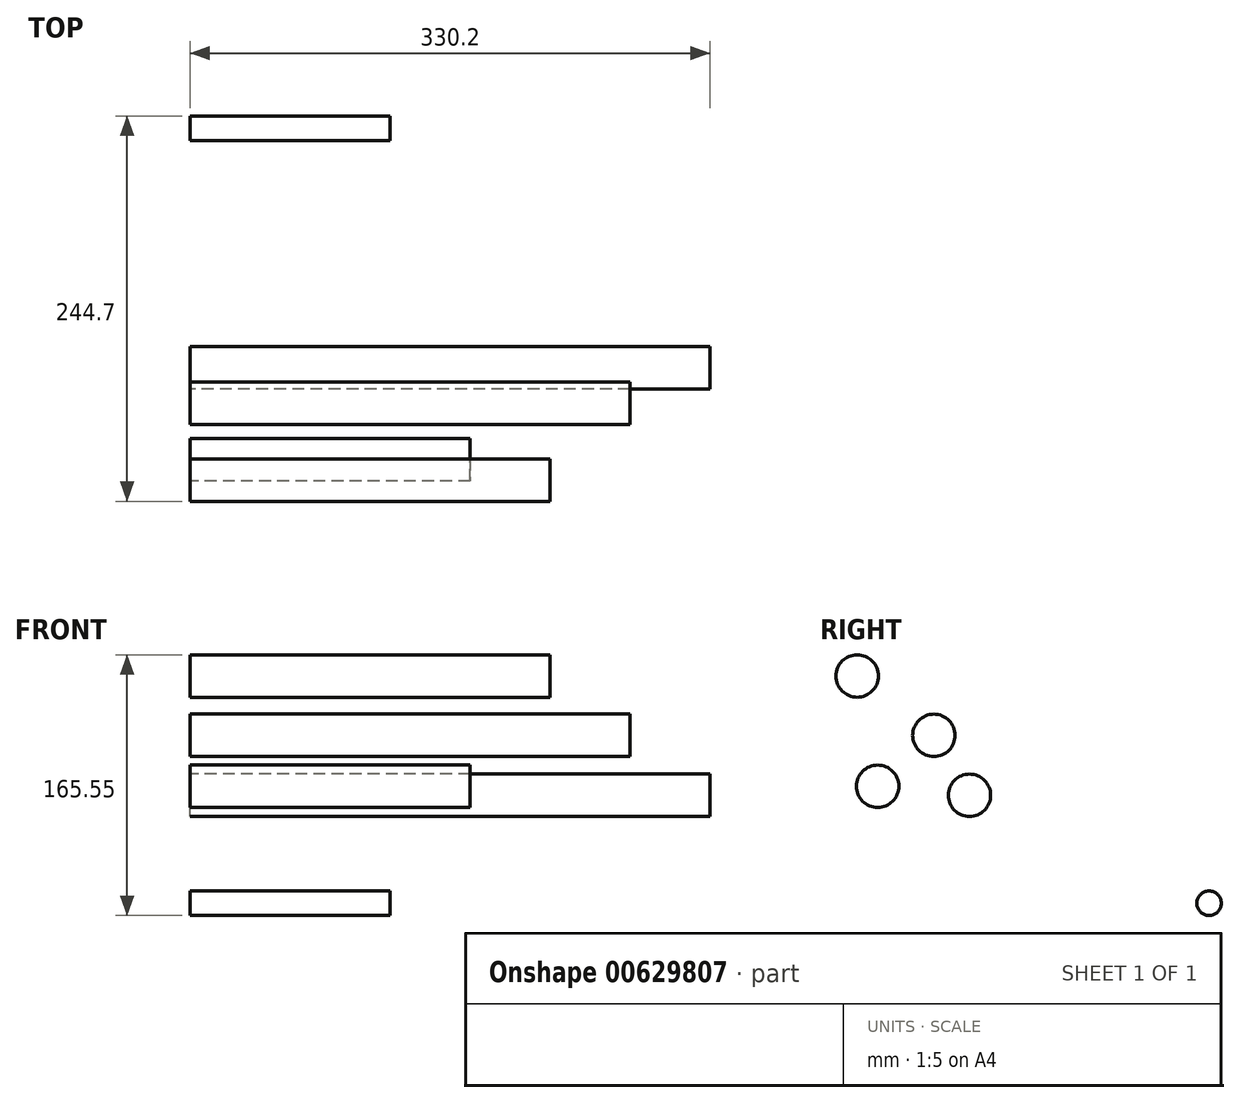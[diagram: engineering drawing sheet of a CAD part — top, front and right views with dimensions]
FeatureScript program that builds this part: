
annotation { "Feature Type Name" : "Feature", "Feature Type Description" : "" }
export const myFeature = defineFeature(function(context is Context, id is Id, definition is map)
    precondition{}
    {
        {
            var Q0;
            Q0=qCreatedBy(makeId("Right.planeOp"),FACE);
            var sketch = newSketch(context, id + "F0", { "sketchPlane" : qUnion([Q0])});
            skCircle(sketch, "E0", {"center": v(-9.2, 26.78) * mm, "radius": 13.46 * mm});
            skSolve(sketch);
        }
        {
            var Q0;
            Q0=makeQuery(id+"F0.imprint","IMPRINT",FACE,{"disambiguationData":[TD([[makeQuery(id+"F0.imprint","IMPRINT",EDGE,{"derivedFrom":sQuery(id+"F0.wireOp",EDGE,"E0")}),1.0]])]});
            extrude(context, id + "F1", {"entities" : qUnion([Q0]), "depth" : 279.4 * mm});
        }
        {
            var Q0;
            Q0=qCreatedBy(makeId("Right.planeOp"),FACE);
            var sketch = newSketch(context, id + "F2", { "sketchPlane" : qUnion([Q0])});
            skCircle(sketch, "E1", {"center": v(13.39, -11.3) * mm, "radius": 13.46 * mm});
            skSolve(sketch);
        }
        {
            var Q0;
            Q0=qSketchRegion(id+"F2",true);
            extrude(context, id + "F3", {"entities" : qUnion([Q0]), "depth" : 330.2 * mm});
        }
        {
            var Q0;
            Q0=qCreatedBy(makeId("Right.planeOp"),FACE);
            var sketch = newSketch(context, id + "F4", { "sketchPlane" : qUnion([Q0])});
            skCircle(sketch, "E2", {"center": v(-44.9, -5.57) * mm, "radius": 13.46 * mm});
            skSolve(sketch);
        }
        {
            var Q0;
            Q0=qSketchRegion(id+"F4",true);
            extrude(context, id + "F5", {"entities" : qUnion([Q0]), "depth" : 177.8 * mm});
        }
        {
            var Q0;
            Q0=qCreatedBy(makeId("Right.planeOp"),FACE);
            var sketch = newSketch(context, id + "F6", { "sketchPlane" : qUnion([Q0])});
            skCircle(sketch, "E3", {"center": v(-57.91, 64.48) * mm, "radius": 13.46 * mm});
            skSolve(sketch);
        }
        {
            var Q0;
            Q0=qSketchRegion(id+"F6",true);
            extrude(context, id + "F7", {"entities" : qUnion([Q0]), "depth" : 228.6 * mm});
        }
        {
            var Q0;
            Q0=qCreatedBy(makeId("Right.planeOp"),FACE);
            var sketch = newSketch(context, id + "F8", { "sketchPlane" : qUnion([Q0])});
            skCircle(sketch, "E4", {"center": v(-65.2, -44.58) * mm, "radius": 9.92 * mm});
            skLineSegment(sketch, "E5", {"start": v(-78.1, -17.77) * mm, "end": v(-53.92, -17.77) * mm});
            skLineSegment(sketch, "E6", {"start": v(-65.2, -44.58) * mm, "end": v(-66, -17.77) * mm});
            skSolve(sketch);
        }
        {
            var Q0;
            Q0=qSketchRegion(id+"F8",true);
            var Q1;
            Q1=sQuery(id+"F8.wireOp",EDGE,"E5");
            revolve(context, id + "F9", {"entities" : qUnion([Q0]), "axis" : qUnion([Q1]), "revolveType" : RevolveType.FULL});
        }
        {
            var Q0;
            Q0=makeQuery(id+"F9.opRevolve","SWEPT_BODY",BODY,{"disambiguationData":[OSD([sQuery(id+"F8.wireOp",EDGE,"E4")])]});
            deleteBodies(context, id + "F10", {"entities" : qUnion([Q0])});
        }
        {
            var Q0;
            Q0=qCreatedBy(makeId("Right.planeOp"),FACE);
            var sketch = newSketch(context, id + "F11", { "sketchPlane" : qUnion([Q0])});
            skCircle(sketch, "E7", {"center": v(165.58, -79.86) * mm, "radius": 7.75 * mm});
            skSolve(sketch);
        }
        {
            var Q0;
            Q0=makeQuery(id+"F11.imprint","IMPRINT",FACE,{"disambiguationData":[TD([[makeQuery(id+"F11.imprint","IMPRINT",EDGE,{"derivedFrom":sQuery(id+"F11.wireOp",EDGE,"E7")}),1.0]])]});
            extrude(context, id + "F12", {"entities" : qUnion([Q0]), "depth" : 127 * mm});
        }
    });
